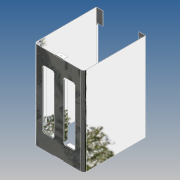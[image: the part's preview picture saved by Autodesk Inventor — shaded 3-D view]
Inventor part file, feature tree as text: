
AUTODESK INVENTOR PART (.ipt)
format: ipt  version: 2016 (Build 200138000, 138)  size: 551,936 bytes
history: native  units: mm
features: sheet_metal_op x28, other x15, sketch x14, reference x1
ambient origin geometry x8: Origin, YZ Plane, XZ Plane, XY Plane, X Axis, Y Axis, Z Axis, Center Point
bodies: Solid1 (feature_tree)
feature tree (58):
  sheet_metal_op  "Face1"
  sheet_metal_op  "Flange1"
  sheet_metal_op  "Flange4"
  sheet_metal_op  "Flange5"
  sheet_metal_op  "Flange6"
  sheet_metal_op  "Flange7"
  sheet_metal_op  "Flange8"
  sheet_metal_op  "Flange9"
  sheet_metal_op  "Flange10"
  sheet_metal_op  "Flange11"
  sketch  "Sketch1"  dims[d0=195.0mm]
  other  "Plate1"
  sketch  "Sketch2"  dims[d1=110.0mm]
  other  "Plate2"
  sheet_metal_op  "Bend1"
  sheet_metal_op  "Corner1"
  sketch  "Sketch9"  dims[d2=0.5mm]
  other  "Plate5"
  sheet_metal_op  "Bend4"
  sheet_metal_op  "Corner4"
  sketch  "Sketch10"  dims[d3=0.5mm]
  other  "Plate6"
  sheet_metal_op  "Bend5"
  sheet_metal_op  "Corner5"
  sketch  "Sketch11"  dims[d4=0.25mm]
  other  "Plate7"
  sheet_metal_op  "Bend6"
  sheet_metal_op  "Corner6"
  sketch  "Sketch12"  dims[d5=1.0mm]
  other  "Plate8"
  sheet_metal_op  "Bend7"
  sheet_metal_op  "Corner7"
  sketch  "Sketch13"  dims[d6=0.5mm]
  other  "Plate9"
  sheet_metal_op  "Bend8"
  sheet_metal_op  "Corner8"
  sketch  "Sketch14"  dims[d7=139.0mm d8=90.0deg d9=6.0mm]
  other  "Plate10"
  sheet_metal_op  "Bend9"
  sheet_metal_op  "Corner9"
  sketch  "Sketch15"  dims[d10=2.0mm]
  sketch  "Sketch16"  dims[d11=0.5mm]
  sketch  "Sketch17"  dims[d12=0.5mm]
  other  "Plate11"
  sheet_metal_op  "Bend10"
  sheet_metal_op  "Corner10"
  sketch  "Sketch18"  dims[d40=0.5mm]
  other  "Plate12"
  sheet_metal_op  "Bend11"
  sheet_metal_op  "Corner11"
  sketch  "Sketch19"  dims[d41=0.25mm]
  sketch  "Sketch20"  dims[d42=1.0mm d43=0.5mm d44=15.0mm d45=90.0deg d46=0.5mm d47=0.0mm d48=160.0mm d49=2.0mm d50=0.5mm d51=0.5mm d52=0.5mm d53=0.25mm d54=1.0mm d55=0.5mm d56=15.0mm d57=90.0deg d58=0.5mm d59=0.0mm d60=160.0mm d61=2.0mm d62=0.5mm d63=0.5mm d64=0.5mm d65=0.25mm d66=1.0mm d67=0.5mm d68=15.0mm d69=90.0deg d70=0.5mm d71=130.0mm d72=0.0mm d73=2.0mm d74=0.5mm d75=0.5mm d76=0.5mm d77=0.25mm d78=1.0mm d79=0.5mm d80=15.0mm d81=90.0deg d82=0.5mm d83=130.0mm d84=0.0mm d85=2.0mm d86=0.5mm d87=0.5mm d88=0.5mm d89=0.25mm d90=1.0mm d91=0.5mm d92=5.0mm d93=90.0deg d94=0.5mm d95=2.0mm d96=0.5mm d97=0.5mm d98=0.5mm d99=0.25mm d100=1.0mm d101=0.5mm d102=5.0mm d103=90.0deg d104=0.5mm d105=2.0mm d106=0.5mm d107=0.5mm d108=4.0mm d109=11.0mm d110=4.0mm d111=4.0mm d112=11.0mm d113=0.5mm d114=0.0mm d115=26.0mm d116=130.0mm d117=20.5mm d118=10.25mm d119=5.0mm d120=0.5mm d121=0.0mm d122=0.5mm d123=0.25mm d124=1.0mm d125=0.5mm d126=9.0mm d127=90.0deg d128=0.5mm d129=2.0mm d130=0.5mm d131=0.5mm d132=0.5mm d133=0.25mm d134=1.0mm d135=0.5mm d136=10.6mm d137=90.0deg d138=0.5mm d139=18.0mm d140=18.5mm d141=2.0mm d142=0.5mm d143=0.5mm d144=2.5mm d145=0.5mm d146=0.0mm d147=0.5mm d148=0.0mm]
  reference  "Reference1"
  other  "Cut3"
  other  "Cut2"
  other  "Cut4"
  other  "Cut5"
  other  "Definition1"
